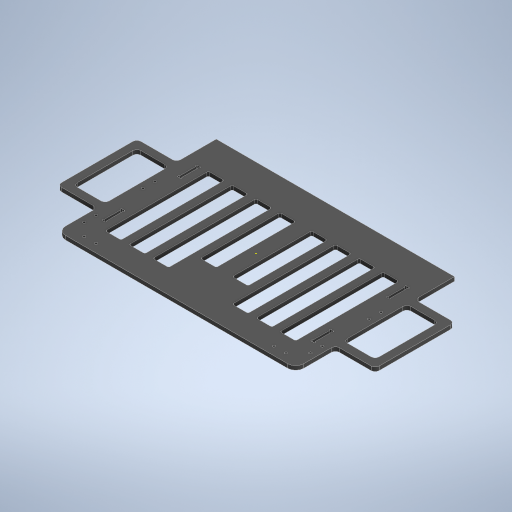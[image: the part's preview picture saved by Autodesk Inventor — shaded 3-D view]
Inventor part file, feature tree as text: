
AUTODESK INVENTOR PART (.ipt)
format: ipt  version: 2024.3 (Build 283343000, 343)  size: 594,944 bytes
history: native  units: mm
features: sketch x6, extrude x5, fillet x3, other x1, projected_geometry x1
ambient origin geometry x8: Origin, YZ Plane, XZ Plane, XY Plane, X Axis, Y Axis, Z Axis, Center Point
bodies: Body1 (feature_tree)
feature tree (16):
  other  "ソリッド1"
  extrude  "押し出し1"  Depth=190.0mm
  extrude  "押し出し4"  Depth=300.0mm
  sketch  "スケッチ4"
  extrude  "押し出し13"  Depth=5.0mm TaperAngle=0.0deg
  fillet  "フィレット3"  Radius=142.5mm
  extrude  "押し出し18"  Depth=285.0mm
  extrude  "押し出し19"  Depth=3.2mm
  fillet  "フィレット11"  Radius=3.2mm
  fillet  "フィレット12"  Radius=21.0mm
  sketch  "スケッチ1"
  sketch  "スケッチ2"
  sketch  "スケッチ14"
  projected_geometry  "投影ループ5"
  sketch  "スケッチ19"
  sketch  "スケッチ20"
